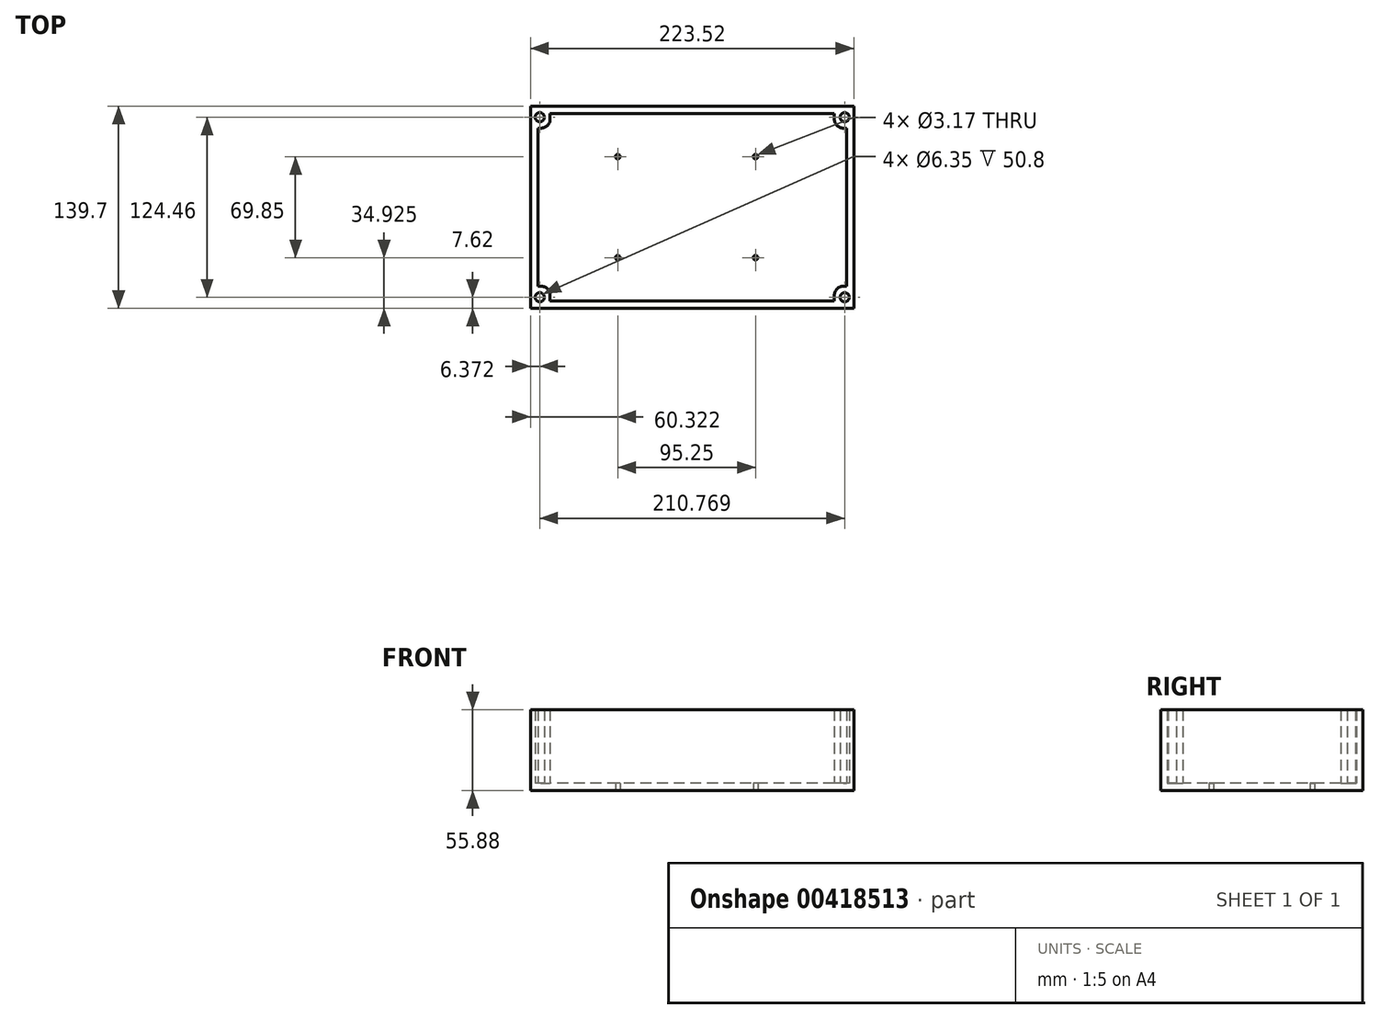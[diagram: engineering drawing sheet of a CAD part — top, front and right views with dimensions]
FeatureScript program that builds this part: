
annotation { "Feature Type Name" : "Feature", "Feature Type Description" : "" }
export const myFeature = defineFeature(function(context is Context, id is Id, definition is map)
    precondition{}
    {
        {
            var Q0;
            Q0=qCreatedBy(makeId("Top.planeOp"),FACE);
            var sketch = newSketch(context, id + "F0", { "sketchPlane" : qUnion([Q0])});
            skLineSegment(sketch, "E0.bottom", {"start": v(-237.1, 139.7) * mm, "end": v(-13.58, 139.7) * mm});
            skLineSegment(sketch, "E0.top", {"start": v(-237.1, 0) * mm, "end": v(-13.58, 0) * mm});
            skLineSegment(sketch, "E0.left", {"start": v(-237.1, 139.7) * mm, "end": v(-237.1, 0) * mm});
            skLineSegment(sketch, "E0.right", {"start": v(-13.58, 139.7) * mm, "end": v(-13.58, 0) * mm});
            skCircle(sketch, "E1", {"center": v(-176.78, 104.78) * mm, "radius": 1.59 * mm});
            skCircle(sketch, "E2.MirrorC", {"center": v(-81.53, 104.78) * mm, "radius": 1.59 * mm});
            skCircle(sketch, "E3.MirrorC", {"center": v(-176.78, 34.92) * mm, "radius": 1.59 * mm});
            skCircle(sketch, "E4.MirrorC", {"center": v(-81.53, 34.92) * mm, "radius": 1.59 * mm});
            skSolve(sketch);
        }
        {
            var Q0;
            Q0 = qSketchRegion(id + "F0", true);
            extrude(context, id + "F1", {"entities" : qUnion([Q0]), "depth" : 5.08 * mm});
        }
        {
            var Q0;
            Q0=makeQuery(id+"F1.opExtrude","CAP_FACE",FACE,{"disambiguationData":[OSD([sQuery(id+"F0.wireOp",EDGE,"E0.bottom"),sQuery(id+"F0.wireOp",EDGE,"E0.top"),sQuery(id+"F0.wireOp",EDGE,"E0.left"),sQuery(id+"F0.wireOp",EDGE,"E0.right")])],"isStart":false});
            var sketch = newSketch(context, id + "F2", { "sketchPlane" : qUnion([Q0])});
            skLineSegment(sketch, "E5.bottom", {"start": v(-237.1, 139.7) * mm, "end": v(-229.48, 139.7) * mm});
            skLineSegment(sketch, "E5.left", {"start": v(-237.1, 139.7) * mm, "end": v(-237.1, 132.08) * mm});
            skCircle(sketch, "E6", {"center": v(-230.73, 132.08) * mm, "radius": 3.17 * mm});
            skLineSegment(sketch, "E7.bottom", {"start": v(-237.1, 139.7) * mm, "end": v(-221.86, 139.7) * mm});
            skLineSegment(sketch, "E7.left", {"start": v(-237.1, 139.7) * mm, "end": v(-237.1, 124.46) * mm});
            skLineSegment(sketch, "E8.left", {"start": v(-237.1, 124.46) * mm, "end": v(-237.1, 0) * mm});
            skLineSegment(sketch, "E9", {"start": v(-232.02, 124.46) * mm, "end": v(-232.02, 15.24) * mm});
            skLineSegment(sketch, "E10.bottom", {"start": v(-125.34, 134.62) * mm, "end": v(-223.55, 134.62) * mm});
            skLineSegment(sketch, "E10.top", {"start": v(-125.34, 139.7) * mm, "end": v(-221.86, 139.7) * mm});
            skLineSegment(sketch, "E11", {"start": v(-223.55, 134.62) * mm, "end": v(-223.55, 130.81) * mm});
            skLineSegment(sketch, "E12", {"start": v(-229.9, 124.46) * mm, "end": v(-232.02, 124.46) * mm});
            skPoint(sketch, "E13.visualSharp", {"position": v(-223.55, 124.46) * mm});
            skArc(sketch, "E13.filletArc", {"start": v(-229.9, 124.46) * mm, "mid": v(-225.41, 126.32) * mm, "end": v(-223.55, 130.81) * mm});
            skLineSegment(sketch, "E14.MirrorCS", {"start": v(-27.13, 134.62) * mm, "end": v(-27.13, 130.81) * mm});
            skLineSegment(sketch, "E15.MirrorCS", {"start": v(-13.58, 139.7) * mm, "end": v(-28.82, 139.7) * mm});
            skLineSegment(sketch, "E16.MirrorCS", {"start": v(-13.58, 139.7) * mm, "end": v(-21.2, 139.7) * mm});
            skLineSegment(sketch, "E17.MirrorCS", {"start": v(-20.78, 124.46) * mm, "end": v(-18.66, 124.46) * mm});
            skCircle(sketch, "E18.MirrorC", {"center": v(-19.96, 132.08) * mm, "radius": 3.17 * mm});
            skLineSegment(sketch, "E19.MirrorCS", {"start": v(-13.58, 139.7) * mm, "end": v(-13.58, 132.08) * mm});
            skLineSegment(sketch, "E20.MirrorCS", {"start": v(-13.58, 139.7) * mm, "end": v(-13.58, 124.46) * mm});
            skArc(sketch, "E21.MirrorCS", {"start": v(-20.78, 124.46) * mm, "mid": v(-25.27, 126.32) * mm, "end": v(-27.13, 130.81) * mm});
            skPoint(sketch, "E22.MirrorP", {"position": v(-27.13, 124.46) * mm});
            skLineSegment(sketch, "E23.MirrorCS", {"start": v(-13.58, 124.46) * mm, "end": v(-13.58, 0) * mm});
            skLineSegment(sketch, "E24.MirrorCS", {"start": v(-125.34, 134.62) * mm, "end": v(-27.13, 134.62) * mm});
            skLineSegment(sketch, "E25.MirrorCS", {"start": v(-125.34, 139.7) * mm, "end": v(-28.82, 139.7) * mm});
            skLineSegment(sketch, "E26.MirrorCS", {"start": v(-18.66, 124.46) * mm, "end": v(-18.66, 15.24) * mm});
            skLineSegment(sketch, "E27.MirrorCS", {"start": v(-20.78, 15.24) * mm, "end": v(-18.66, 15.24) * mm});
            skLineSegment(sketch, "E28.MirrorCS", {"start": v(-229.9, 15.24) * mm, "end": v(-232.02, 15.24) * mm});
            skLineSegment(sketch, "E29.MirrorCS", {"start": v(-27.13, 5.08) * mm, "end": v(-27.13, 8.89) * mm});
            skLineSegment(sketch, "E30.MirrorCS", {"start": v(-223.55, 5.08) * mm, "end": v(-223.55, 8.89) * mm});
            skArc(sketch, "E31.MirrorCS", {"start": v(-20.78, 15.24) * mm, "mid": v(-25.27, 13.38) * mm, "end": v(-27.13, 8.89) * mm});
            skCircle(sketch, "E32.MirrorC", {"center": v(-19.96, 7.62) * mm, "radius": 3.17 * mm});
            skLineSegment(sketch, "E33.MirrorCS", {"start": v(-237.1, 0) * mm, "end": v(-221.86, 0) * mm});
            skLineSegment(sketch, "E34.MirrorCS", {"start": v(-13.58, 0) * mm, "end": v(-13.58, 15.24) * mm});
            skLineSegment(sketch, "E35.MirrorCS", {"start": v(-237.1, 0) * mm, "end": v(-237.1, 15.24) * mm});
            skLineSegment(sketch, "E36.MirrorCS", {"start": v(-13.58, 0) * mm, "end": v(-13.58, 7.62) * mm});
            skLineSegment(sketch, "E37.MirrorCS", {"start": v(-13.58, 0) * mm, "end": v(-21.2, 0) * mm});
            skLineSegment(sketch, "E38.MirrorCS", {"start": v(-237.1, 0) * mm, "end": v(-229.48, 0) * mm});
            skLineSegment(sketch, "E39.MirrorCS", {"start": v(-237.1, 0) * mm, "end": v(-237.1, 7.62) * mm});
            skArc(sketch, "E40.MirrorCS", {"start": v(-229.9, 15.24) * mm, "mid": v(-225.41, 13.38) * mm, "end": v(-223.55, 8.89) * mm});
            skLineSegment(sketch, "E41.MirrorCS", {"start": v(-13.58, 0) * mm, "end": v(-28.82, 0) * mm});
            skCircle(sketch, "E42.MirrorC", {"center": v(-230.73, 7.62) * mm, "radius": 3.17 * mm});
            skLineSegment(sketch, "E43.MirrorCS", {"start": v(-125.34, 5.08) * mm, "end": v(-27.13, 5.08) * mm});
            skLineSegment(sketch, "E44.MirrorCS", {"start": v(-125.34, 5.08) * mm, "end": v(-223.55, 5.08) * mm});
            skPoint(sketch, "E45.MirrorP", {"position": v(-27.13, 15.24) * mm});
            skLineSegment(sketch, "E46.MirrorCS", {"start": v(-125.34, 0) * mm, "end": v(-221.86, 0) * mm});
            skLineSegment(sketch, "E47.MirrorCS", {"start": v(-125.34, 0) * mm, "end": v(-28.82, 0) * mm});
            skPoint(sketch, "E48.MirrorP", {"position": v(-223.55, 15.24) * mm});
            skSolve(sketch);
        }
        {
            var Q0;
            Q0 = qSketchRegion(id + "F2", true);
            extrude(context, id + "F3", {"entities" : qUnion([Q0]), "operationType" : NewBodyOperationType.ADD, "depth" : 50.8 * mm});
        }
    });
